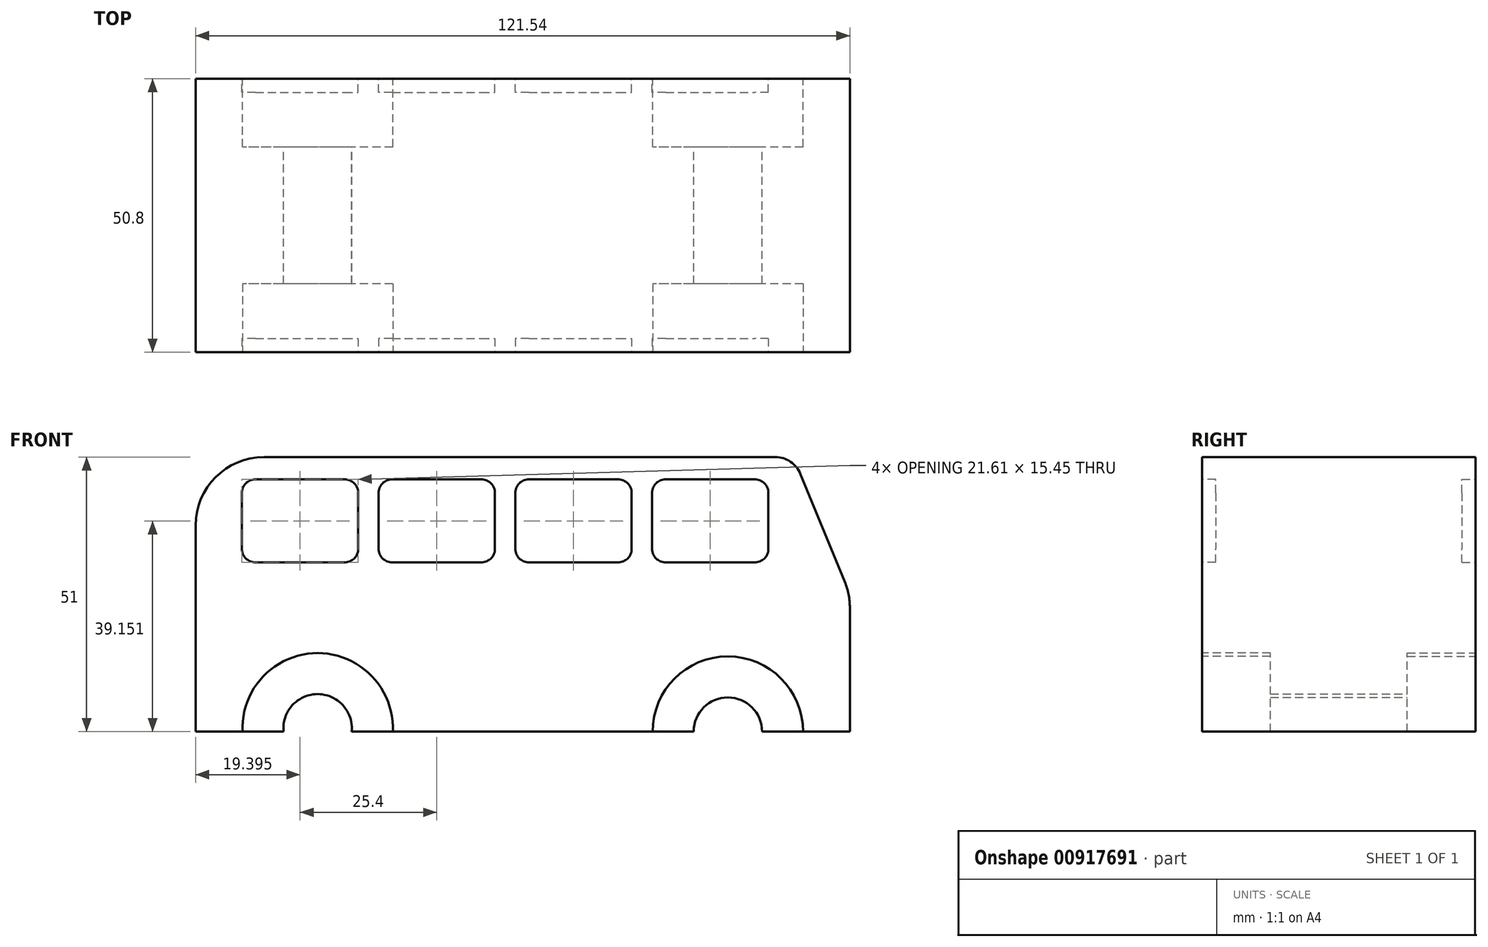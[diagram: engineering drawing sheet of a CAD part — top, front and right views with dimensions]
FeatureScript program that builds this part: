
annotation { "Feature Type Name" : "Feature", "Feature Type Description" : "" }
export const myFeature = defineFeature(function(context is Context, id is Id, definition is map)
    precondition{}
    {
        {
            var Q0;
            Q0=qCreatedBy(makeId("Front.planeOp"),FACE);
            var sketch = newSketch(context, id + "F0", { "sketchPlane" : qUnion([Q0])});
            skLineSegment(sketch, "E0.bottom", {"start": v(46.9, 25.5) * mm, "end": v(-48.07, 25.5) * mm});
            skLineSegment(sketch, "E0.top", {"start": v(60.77, -25.5) * mm, "end": v(44.45, -25.5) * mm});
            skLineSegment(sketch, "E0.left", {"start": v(60.77, -2.5) * mm, "end": v(60.77, -25.5) * mm});
            skLineSegment(sketch, "E0.right", {"start": v(-60.77, 12.8) * mm, "end": v(-60.77, -25.5) * mm});
            skPoint(sketch, "E0.middle", {"position": v(0, 0) * mm});
            skLineSegment(sketch, "E1", {"start": v(59.82, 2.31) * mm, "end": v(51.6, 22.35) * mm});
            skPoint(sketch, "E2.orphan", {"position": v(60.77, 25.5) * mm});
            skPoint(sketch, "E3.visualSharp", {"position": v(-60.77, 25.5) * mm});
            skArc(sketch, "E3.filletArc", {"start": v(-48.07, 25.5) * mm, "mid": v(-57.05, 21.78) * mm, "end": v(-60.77, 12.8) * mm});
            skPoint(sketch, "E4.visualSharp", {"position": v(50.31, 25.5) * mm});
            skArc(sketch, "E4.filletArc", {"start": v(51.6, 22.35) * mm, "mid": v(49.74, 24.64) * mm, "end": v(46.9, 25.5) * mm});
            skPoint(sketch, "E5.visualSharp", {"position": v(60.77, 0) * mm});
            skArc(sketch, "E5.filletArc", {"start": v(60.77, -2.5) * mm, "mid": v(60.53, -0.05) * mm, "end": v(59.82, 2.31) * mm});
            skLineSegment(sketch, "E6", {"start": v(0, 0) * mm, "end": v(0, -49.77) * mm, "construction": true});
            skLineSegment(sketch, "E7.0", {"start": v(38.1, 0) * mm, "end": v(38.1, -49.77) * mm, "construction": true});
            skLineSegment(sketch, "E8.0", {"start": v(-38.1, 0) * mm, "end": v(-38.1, -49.77) * mm, "construction": true});
            skArc(sketch, "E9", {"start": v(-44.42, -25.5) * mm, "mid": v(-38.1, -18.53) * mm, "end": v(-31.78, -25.5) * mm});
            skArc(sketch, "E10", {"start": v(44.45, -25.5) * mm, "mid": v(38.1, -19.15) * mm, "end": v(31.75, -25.5) * mm});
            skLineSegment(sketch, "E11.trimOffspring", {"start": v(-44.42, -25.5) * mm, "end": v(-60.77, -25.5) * mm});
            skLineSegment(sketch, "E12.trimOffspring", {"start": v(31.75, -25.5) * mm, "end": v(-31.78, -25.5) * mm});
            skSolve(sketch);
        }
        {
            var Q0;
            Q0=makeQuery(id+"F0.imprint","IMPRINT",FACE,{"disambiguationData":[TD([[makeQuery(id+"F0.imprint","IMPRINT",EDGE,{"derivedFrom":sQuery(id+"F0.wireOp",EDGE,"E0.bottom")}),1.0]])]});
            extrude(context, id + "F1", {"entities" : qUnion([Q0]), "depth" : 25.4 * mm, "offsetDistance" : 25.4 * mm});
        }
        {
            var Q0;
            Q0=makeQuery(id+"F1.opExtrude","CAP_FACE",FACE,{"disambiguationData":[OSD([sQuery(id+"F0.wireOp",EDGE,"E0.bottom"),sQuery(id+"F0.wireOp",EDGE,"E0.top"),sQuery(id+"F0.wireOp",EDGE,"E0.left"),sQuery(id+"F0.wireOp",EDGE,"E0.right"),sQuery(id+"F0.wireOp",EDGE,"E1"),sQuery(id+"F0.wireOp",EDGE,"E3.filletArc"),sQuery(id+"F0.wireOp",EDGE,"E4.filletArc"),sQuery(id+"F0.wireOp",EDGE,"E5.filletArc"),sQuery(id+"F0.wireOp",EDGE,"E9"),sQuery(id+"F0.wireOp",EDGE,"E10"),sQuery(id+"F0.wireOp",EDGE,"E11.trimOffspring"),sQuery(id+"F0.wireOp",EDGE,"E12.trimOffspring")])],"isStart":false});
            var sketch = newSketch(context, id + "F2", { "sketchPlane" : qUnion([Q0])});
            skLineSegment(sketch, "E13.bottom", {"start": v(26.56, 21.38) * mm, "end": v(43.1, 21.38) * mm});
            skLineSegment(sketch, "E13.top", {"start": v(26.56, 5.93) * mm, "end": v(43.1, 5.93) * mm});
            skLineSegment(sketch, "E13.left", {"start": v(24.02, 18.84) * mm, "end": v(24.02, 8.47) * mm});
            skLineSegment(sketch, "E13.right", {"start": v(45.63, 18.84) * mm, "end": v(45.63, 8.47) * mm});
            skPoint(sketch, "E14.visualSharp", {"position": v(24.02, 21.38) * mm});
            skArc(sketch, "E14.filletArc", {"start": v(26.56, 21.38) * mm, "mid": v(24.76, 20.63) * mm, "end": v(24.02, 18.84) * mm});
            skPoint(sketch, "E15.visualSharp", {"position": v(45.63, 21.38) * mm});
            skArc(sketch, "E15.filletArc", {"start": v(45.63, 18.84) * mm, "mid": v(44.89, 20.63) * mm, "end": v(43.1, 21.38) * mm});
            skPoint(sketch, "E16.visualSharp", {"position": v(45.63, 5.93) * mm});
            skArc(sketch, "E16.filletArc", {"start": v(43.1, 5.93) * mm, "mid": v(44.89, 6.67) * mm, "end": v(45.63, 8.47) * mm});
            skPoint(sketch, "E17.visualSharp", {"position": v(24.02, 5.93) * mm});
            skArc(sketch, "E17.filletArc", {"start": v(24.02, 8.47) * mm, "mid": v(24.76, 6.67) * mm, "end": v(26.56, 5.93) * mm});
            skLineSegment(sketch, "E18.1.0.0", {"start": v(20.23, 18.84) * mm, "end": v(20.23, 8.47) * mm});
            skPoint(sketch, "E18.1.0.1", {"position": v(20.23, 5.93) * mm});
            skLineSegment(sketch, "E18.1.0.2", {"start": v(1.16, 21.38) * mm, "end": v(17.7, 21.38) * mm});
            skPoint(sketch, "E18.1.0.3", {"position": v(-1.38, 5.93) * mm});
            skLineSegment(sketch, "E18.1.0.4", {"start": v(-1.38, 18.84) * mm, "end": v(-1.38, 8.47) * mm});
            skLineSegment(sketch, "E18.1.0.5", {"start": v(1.16, 5.93) * mm, "end": v(17.7, 5.93) * mm});
            skPoint(sketch, "E18.1.0.6", {"position": v(-1.38, 21.38) * mm});
            skPoint(sketch, "E18.1.0.7", {"position": v(20.23, 21.38) * mm});
            skArc(sketch, "E18.1.0.8", {"start": v(17.7, 5.93) * mm, "mid": v(19.49, 6.67) * mm, "end": v(20.23, 8.47) * mm});
            skArc(sketch, "E18.1.0.9", {"start": v(20.23, 18.84) * mm, "mid": v(19.49, 20.63) * mm, "end": v(17.7, 21.38) * mm});
            skArc(sketch, "E18.1.0.10", {"start": v(-1.38, 8.47) * mm, "mid": v(-0.64, 6.67) * mm, "end": v(1.16, 5.93) * mm});
            skArc(sketch, "E18.1.0.11", {"start": v(1.16, 21.38) * mm, "mid": v(-0.64, 20.63) * mm, "end": v(-1.38, 18.84) * mm});
            skLineSegment(sketch, "E18.2.0.0", {"start": v(-5.17, 18.84) * mm, "end": v(-5.17, 8.47) * mm});
            skPoint(sketch, "E18.2.0.1", {"position": v(-5.17, 5.93) * mm});
            skLineSegment(sketch, "E18.2.0.2", {"start": v(-24.24, 21.38) * mm, "end": v(-7.7, 21.38) * mm});
            skPoint(sketch, "E18.2.0.3", {"position": v(-26.78, 5.93) * mm});
            skLineSegment(sketch, "E18.2.0.4", {"start": v(-26.78, 18.84) * mm, "end": v(-26.78, 8.47) * mm});
            skLineSegment(sketch, "E18.2.0.5", {"start": v(-24.24, 5.93) * mm, "end": v(-7.7, 5.93) * mm});
            skPoint(sketch, "E18.2.0.6", {"position": v(-26.78, 21.38) * mm});
            skPoint(sketch, "E18.2.0.7", {"position": v(-5.17, 21.38) * mm});
            skArc(sketch, "E18.2.0.8", {"start": v(-7.7, 5.93) * mm, "mid": v(-5.91, 6.67) * mm, "end": v(-5.17, 8.47) * mm});
            skArc(sketch, "E18.2.0.9", {"start": v(-5.17, 18.84) * mm, "mid": v(-5.91, 20.63) * mm, "end": v(-7.7, 21.38) * mm});
            skArc(sketch, "E18.2.0.10", {"start": v(-26.78, 8.47) * mm, "mid": v(-26.04, 6.67) * mm, "end": v(-24.24, 5.93) * mm});
            skArc(sketch, "E18.2.0.11", {"start": v(-24.24, 21.38) * mm, "mid": v(-26.04, 20.63) * mm, "end": v(-26.78, 18.84) * mm});
            skLineSegment(sketch, "E18.3.0.0", {"start": v(-30.57, 18.84) * mm, "end": v(-30.57, 8.47) * mm});
            skPoint(sketch, "E18.3.0.1", {"position": v(-30.57, 5.93) * mm});
            skLineSegment(sketch, "E18.3.0.2", {"start": v(-49.64, 21.38) * mm, "end": v(-33.1, 21.38) * mm});
            skPoint(sketch, "E18.3.0.3", {"position": v(-52.18, 5.93) * mm});
            skLineSegment(sketch, "E18.3.0.4", {"start": v(-52.18, 18.84) * mm, "end": v(-52.18, 8.47) * mm});
            skLineSegment(sketch, "E18.3.0.5", {"start": v(-49.64, 5.93) * mm, "end": v(-33.1, 5.93) * mm});
            skPoint(sketch, "E18.3.0.6", {"position": v(-52.18, 21.38) * mm});
            skPoint(sketch, "E18.3.0.7", {"position": v(-30.57, 21.38) * mm});
            skArc(sketch, "E18.3.0.8", {"start": v(-33.1, 5.93) * mm, "mid": v(-31.31, 6.67) * mm, "end": v(-30.57, 8.47) * mm});
            skArc(sketch, "E18.3.0.9", {"start": v(-30.57, 18.84) * mm, "mid": v(-31.31, 20.63) * mm, "end": v(-33.1, 21.38) * mm});
            skArc(sketch, "E18.3.0.10", {"start": v(-52.18, 8.47) * mm, "mid": v(-51.44, 6.67) * mm, "end": v(-49.64, 5.93) * mm});
            skArc(sketch, "E18.3.0.11", {"start": v(-49.64, 21.38) * mm, "mid": v(-51.44, 20.63) * mm, "end": v(-52.18, 18.84) * mm});
            skLineSegment(sketch, "E18.direction1", {"start": v(24.02, 5.93) * mm, "end": v(-1.38, 5.93) * mm, "construction": true});
            skSolve(sketch);
        }
        {
            var Q0;
            Q0=makeQuery(id+"F2.imprint","IMPRINT",FACE,{"disambiguationData":[TD([[makeQuery(id+"F2.imprint","IMPRINT",EDGE,{"derivedFrom":sQuery(id+"F2.wireOp",EDGE,"E13.bottom")}),-1.0]])]});
            var Q1;
            Q1=makeQuery(id+"F2.imprint","IMPRINT",FACE,{"disambiguationData":[TD([[makeQuery(id+"F2.imprint","IMPRINT",EDGE,{"derivedFrom":sQuery(id+"F2.wireOp",EDGE,"E18.1.0.0")}),-1.0]])]});
            var Q2;
            Q2=makeQuery(id+"F2.imprint","IMPRINT",FACE,{"disambiguationData":[TD([[makeQuery(id+"F2.imprint","IMPRINT",EDGE,{"derivedFrom":sQuery(id+"F2.wireOp",EDGE,"E18.2.0.0")}),-1.0]])]});
            var Q3;
            Q3=makeQuery(id+"F2.imprint","IMPRINT",FACE,{"disambiguationData":[TD([[makeQuery(id+"F2.imprint","IMPRINT",EDGE,{"derivedFrom":sQuery(id+"F2.wireOp",EDGE,"E18.3.0.0")}),-1.0]])]});
            extrude(context, id + "F3", {"entities" : qUnion([Q0, Q1, Q2, Q3]), "operationType" : NewBodyOperationType.REMOVE, "oppositeDirection" : true, "depth" : 2.54 * mm, "offsetDistance" : 25.4 * mm});
        }
        {
            var Q0;
            Q0=makeQuery(id+"F1.opExtrude","CAP_FACE",FACE,{"disambiguationData":[OSD([sQuery(id+"F0.wireOp",EDGE,"E0.bottom"),sQuery(id+"F0.wireOp",EDGE,"E0.top"),sQuery(id+"F0.wireOp",EDGE,"E0.left"),sQuery(id+"F0.wireOp",EDGE,"E0.right"),sQuery(id+"F0.wireOp",EDGE,"E1"),sQuery(id+"F0.wireOp",EDGE,"E3.filletArc"),sQuery(id+"F0.wireOp",EDGE,"E4.filletArc"),sQuery(id+"F0.wireOp",EDGE,"E5.filletArc"),sQuery(id+"F0.wireOp",EDGE,"E9"),sQuery(id+"F0.wireOp",EDGE,"E10"),sQuery(id+"F0.wireOp",EDGE,"E11.trimOffspring"),sQuery(id+"F0.wireOp",EDGE,"E12.trimOffspring")])],"isStart":false});
            var sketch = newSketch(context, id + "F4", { "sketchPlane" : qUnion([Q0])});
            skCircle(sketch, "E19", {"center": v(-38.1, -24.88) * mm, "radius": 13.97 * mm});
            skCircle(sketch, "E20", {"center": v(38.1, -25.5) * mm, "radius": 13.97 * mm});
            skSolve(sketch);
        }
        {
            var Q0;
            Q0 = qSketchRegion(id + "F4", true);
            extrude(context, id + "F5", {"entities" : qUnion([Q0]), "operationType" : NewBodyOperationType.REMOVE, "oppositeDirection" : true, "depth" : 12.7 * mm, "offsetDistance" : 25.4 * mm});
        }
        {
            var Q0;
            Q0=makeQuery(id+"F1.opExtrude","SWEPT_BODY",BODY,{"disambiguationData":[OSD([sQuery(id+"F0.wireOp",EDGE,"E0.bottom"),sQuery(id+"F0.wireOp",EDGE,"E0.top"),sQuery(id+"F0.wireOp",EDGE,"E0.left"),sQuery(id+"F0.wireOp",EDGE,"E0.right"),sQuery(id+"F0.wireOp",EDGE,"E1"),sQuery(id+"F0.wireOp",EDGE,"E3.filletArc"),sQuery(id+"F0.wireOp",EDGE,"E4.filletArc"),sQuery(id+"F0.wireOp",EDGE,"E5.filletArc"),sQuery(id+"F0.wireOp",EDGE,"E9"),sQuery(id+"F0.wireOp",EDGE,"E10"),sQuery(id+"F0.wireOp",EDGE,"E11.trimOffspring"),sQuery(id+"F0.wireOp",EDGE,"E12.trimOffspring")])]});
            var Q1;
            Q1=qCreatedBy(makeId("Front.planeOp"),FACE);
            mirror(context, id + "F6", {"operationType" : NewBodyOperationType.ADD, "entities" : qUnion([Q0]), "mirrorPlane" : qUnion([Q1])});
        }
    });
